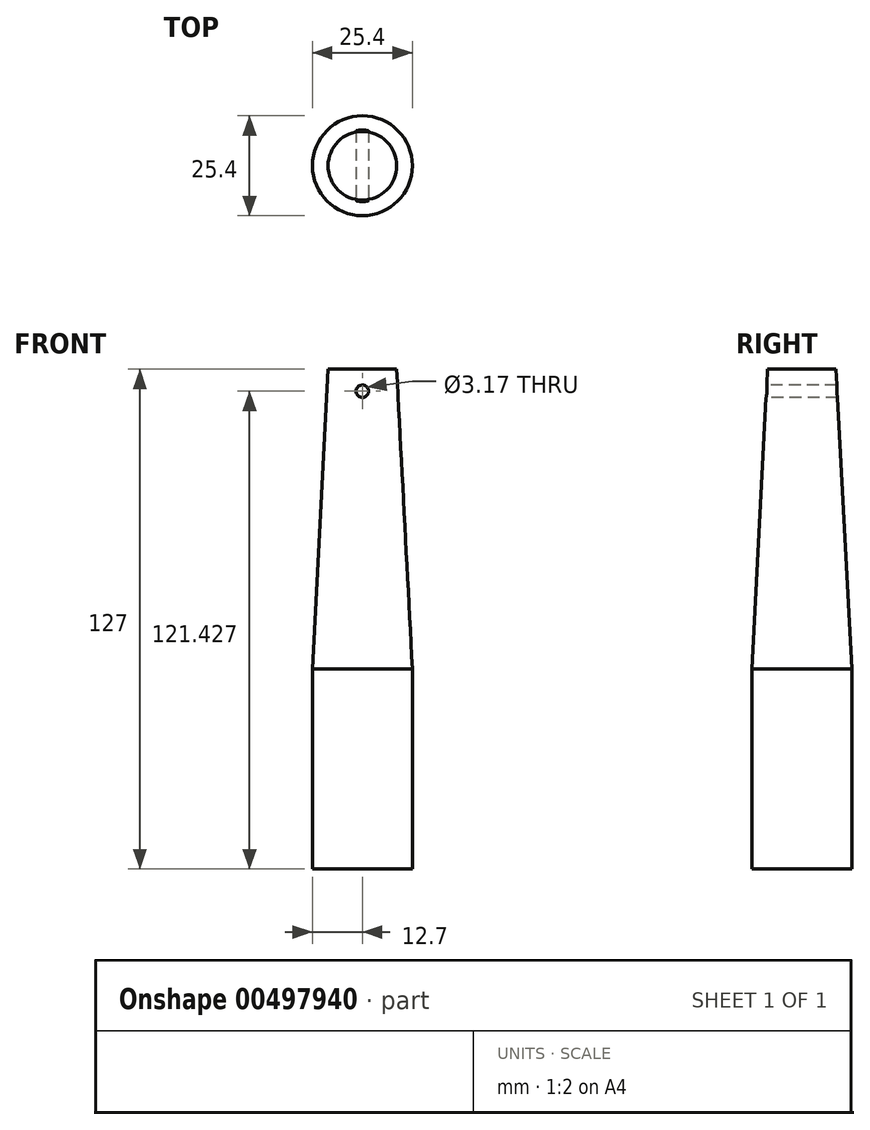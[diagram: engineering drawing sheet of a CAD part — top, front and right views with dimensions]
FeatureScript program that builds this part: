
annotation { "Feature Type Name" : "Feature", "Feature Type Description" : "" }
export const myFeature = defineFeature(function(context is Context, id is Id, definition is map)
    precondition{}
    {
        {
            var Q0;
            Q0=qCreatedBy(makeId("Top.planeOp"),FACE);
            var sketch = newSketch(context, id + "F0", { "sketchPlane" : qUnion([Q0])});
            skCircle(sketch, "E0", {"center": v(0, 0) * mm, "radius": 12.7 * mm});
            skSolve(sketch);
        }
        {
            var Q0;
            Q0 = qSketchRegion(id + "F0", true);
            extrude(context, id + "F1", {"entities" : qUnion([Q0]), "depth" : 76.2 * mm, "hasDraft" : true, "draftAngle" : 3 * degree, "draftPullDirection" : true});
        }
        {
            var Q0;
            Q0=qCreatedBy(makeId("Front.planeOp"),FACE);
            var sketch = newSketch(context, id + "F2", { "sketchPlane" : qUnion([Q0])});
            skCircle(sketch, "E1", {"center": v(0, 70.63) * mm, "radius": 1.59 * mm});
            skSolve(sketch);
        }
        {
            var Q0;
            Q0 = qSketchRegion(id + "F2", true);
            extrude(context, id + "F3", {"entities" : qUnion([Q0]), "operationType" : NewBodyOperationType.REMOVE, "endBound" : BoundingType.SYMMETRIC, "oppositeDirection" : true, "depth" : 127 * mm});
        }
        {
            var Q0;
            Q0=makeQuery(id+"F1.opExtrude","CAP_FACE",FACE,{"disambiguationData":[OSD([sQuery(id+"F0.wireOp",EDGE,"E0")])],"isStart":true});
            extrude(context, id + "F4", {"entities" : qUnion([Q0]), "operationType" : NewBodyOperationType.ADD, "depth" : 50.8 * mm});
        }
    });
